# Revit family: QSC Core 110f
name_source: partatom
category: Generic Models
revit_build: Autodesk Revit 2014 (Build: 20130308_1515(x64)
units: mm (PartAtom-declared; Revit-internal decimal feet)

## types (1)
- QSC Core 110f
    Default Elevation = 0.0"
    Depth = 11.1"
    Description = Flex Channel Audio DSP
    Face Depth = 0.1"
    Height = 1.8"
    Manufacturer = QSC Audio Products, LLC
    Manufacturer URL = www.qscaudio.com
    Model = Q-SYS Core 110f
    Product Documentation Link = http://qsc.com
    Product Page URL = http://qsc.com
    Regulatory Compliance = FCC Part 15B (USA), FCC part 68 / TIA-968-B (USA), JATE (Japan), AS/ACIF S002 (Australia), PTC200 (New Zealand),
ES203 021 (Europe), ANATEL Resolution 473 (Brazil), NOM-151-SCTI (Mexico), PSTN01 (Taiwan), Industry Canada CS-03 (Canada),
CE marked (Europe), UL and C-UL listed (USA & Canada), RCM (Australia), EAC (Eurasian Customs Union) & RoHS Directive (Europe)
    URL = http://qsc.com
    Voltage AC = 100-240 at 50-60 Hz
    Weight Dimensional (kg) = 5.6
    Weight Dimensional (lb) = 12.4
    Weight Product (kg) = 5
    Weight Product (lb) = 11
    Width = 19.0"

## geometry (parser evidence)
native form markers: Blend x1, Sweep x1
no freeform markers — native parametric forms only
